# Revit family: Basin-Under Counter-Caroma Cube 500
name_source: partatom
category: Plumbing Fixtures
revit_build: Autodesk Revit 2014 (Build: 20131024_2115(x64)
units: mm (PartAtom-declared; Revit-internal decimal feet)

## types (1)
- Cube 500
    Assembly Code = D2010310
    Bench Thickness = 20 mm  [stored 0.0656168 ft]
    CW Connection = No
    Default Elevation = 0 mm  [stored 0 ft]
    Depth_ANZRS = 172 mm  [stored 0.564304 ft]
    Description = Caroma Cube 500 Under Counter Basin
    HW Connection = No
    Length_ANZRS = 528 mm  [stored 1.73228 ft]
    Manufacturer = GWA Bathrooms & Kitchens
    Material_ANZRS = Porcelain-White-Caroma
    Model = 683455W
    ModifiedIssue_ANZRS = 20140916 $
    Type Comments = White Only, 12.5L Capacity, Supplied with Overflow Only, Includes flush-fitting white plug and waste
    URL = http://www.caroma.com.au
    Vent Connection = No
    WFU = 1
    Waste = Metal-Chrome-Caroma
    Waste Connection = Yes
    Width_ANZRS = 348 mm  [stored 1.14173 ft]

note: [stored X ft] marks values corroborated as IEEE doubles in the binary element streams (Revit-internal decimal feet)

## geometry (parser evidence)
native form markers: Blend x12, Sweep x1
no freeform markers — native parametric forms only
